# Revit family: AD-S402T - Freespace
name_source: partatom
category: Communication Devices
revit_build: Autodesk Revit 2017 (Build: 20190508_0315(x64)
units: mm (PartAtom-declared; Revit-internal decimal feet)

## family parameters
Always vertical = No
Cut with Voids When Loaded = No
Maintain Annotation Orientation = No
Part Type = Normal
Room Calculation Point = No
Round Connector Dimension = Use Diameter
Shared = No
Work Plane-Based = Yes

## types (1)
- AD-S402T - Freespace
    100V Taps = 60, 30, 15, 16 Ohm Bypass
    70V Taps = 30, 15, 7.5, 16 Ohm Bypass
    Coverage Horizontal = 150.00°
    Coverage Vertical = 35.00°
    Default Elevation = 0 mm  [stored 0 ft]
    Depth = 126 mm
    Description = 2.75" (x4) Columnar Surface Mount Loudspeaker
    Height = 327 mm
    Manufacturer = QSC
    Manufacturer URL = www.qsc.com
    Model = AD-S402T
    Product Documentation Link = https://www.qsc.com
    Product Page URL = https://www.qsc.com
    Regulatory Compliance = UL1480A
    SPL Max = 111
    Sensitivity = 85
    URL = https://www.qsc.com
    Weight Dimensional (kg) = 5
    Weight Dimensional (lb) = 11
    Weight Product (kg) = 3.4
    Weight Product (lb) = 7.5
    Width = 131 mm

note: [stored X ft] marks values corroborated as IEEE doubles in the binary element streams (Revit-internal decimal feet)

## geometry (parser evidence)
native form markers: Blend x4, Sweep x12
no freeform markers — native parametric forms only
